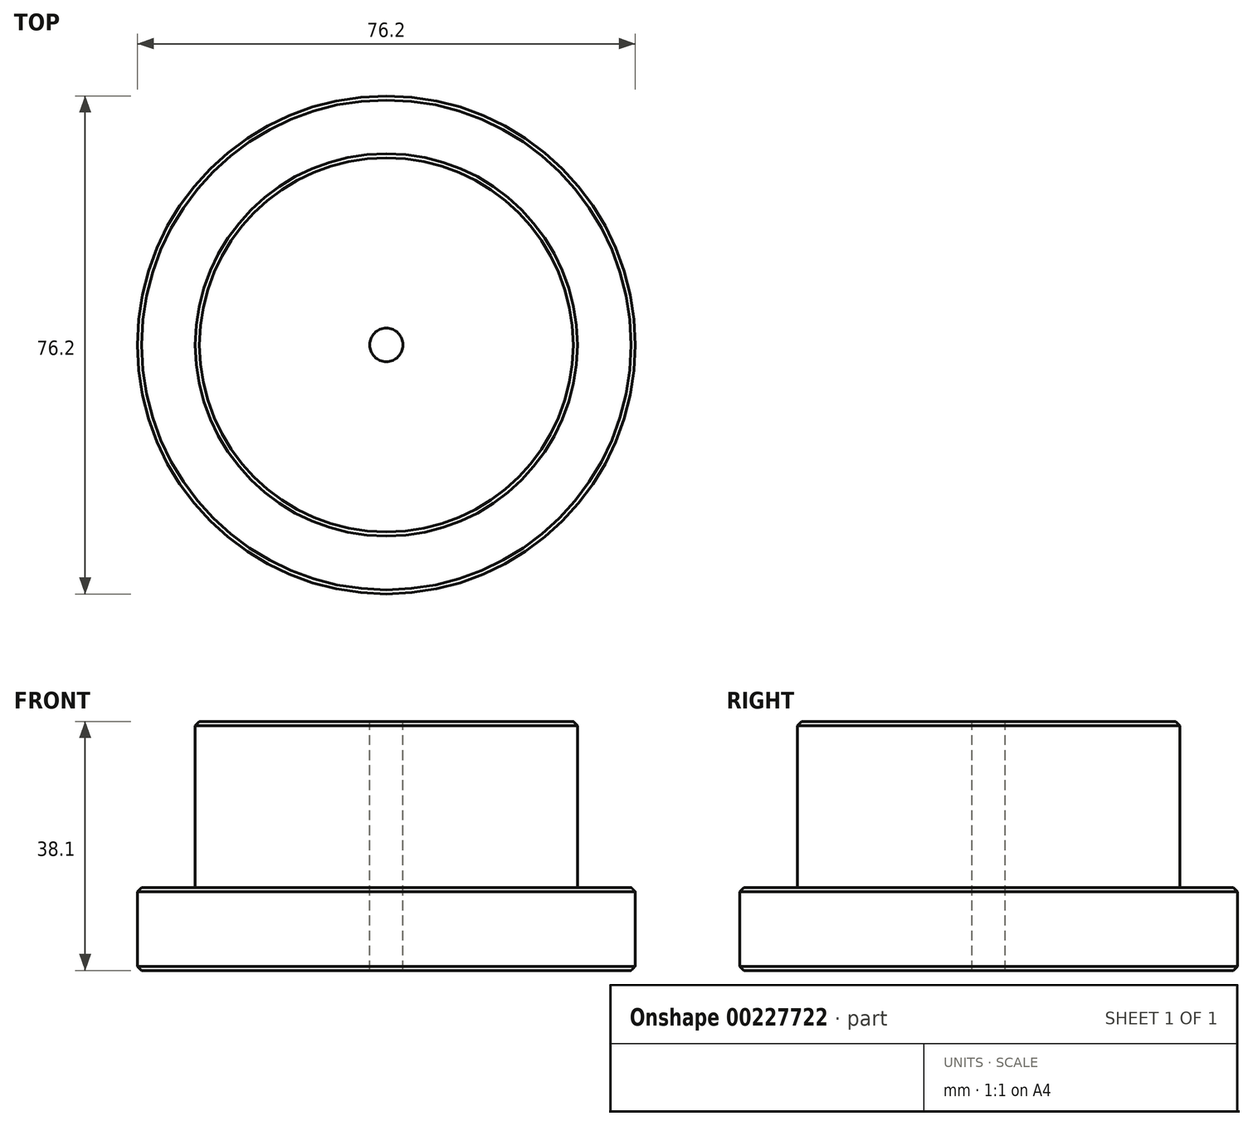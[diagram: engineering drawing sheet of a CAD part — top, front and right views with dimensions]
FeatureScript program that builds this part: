
annotation { "Feature Type Name" : "Feature", "Feature Type Description" : "" }
export const myFeature = defineFeature(function(context is Context, id is Id, definition is map)
    precondition{}
    {
        {
            var Q0;
            Q0=qCreatedBy(makeId("Top.planeOp"),FACE);
            var sketch = newSketch(context, id + "F0", { "sketchPlane" : qUnion([Q0])});
            skCircle(sketch, "E0", {"center": v(0, 0) * mm, "radius": 38.1 * mm});
            skSolve(sketch);
        }
        {
            var Q0;
            Q0 = qSketchRegion(id + "F0", true);
            extrude(context, id + "F1", {"entities" : qUnion([Q0]), "depth" : 12.7 * mm});
        }
        {
            var Q0;
            Q0=makeQuery(id+"F1.opExtrude","CAP_FACE",FACE,{"disambiguationData":[OSD([sQuery(id+"F0.wireOp",EDGE,"E0")])],"isStart":false});
            var sketch = newSketch(context, id + "F2", { "sketchPlane" : qUnion([Q0])});
            skCircle(sketch, "E1", {"center": v(0, 0) * mm, "radius": 29.25 * mm});
            skSolve(sketch);
        }
        {
            var Q0;
            Q0 = qSketchRegion(id + "F2", true);
            extrude(context, id + "F3", {"entities" : qUnion([Q0]), "operationType" : NewBodyOperationType.ADD, "depth" : 25.4 * mm});
        }
        {
            var Q0;
            Q0=makeQuery(id+"F3.opExtrude","CAP_EDGE",EDGE,{"disambiguationData":[OSD([sQuery(id+"F2.wireOp",EDGE,"E1")])],"isStart":false});
            var Q1;
            Q1=makeQuery(id+"F1.opExtrude","CAP_EDGE",EDGE,{"disambiguationData":[OSD([sQuery(id+"F0.wireOp",EDGE,"E0")])],"isStart":false});
            var Q2;
            Q2=makeQuery(id+"F1.opExtrude","CAP_EDGE",EDGE,{"disambiguationData":[OSD([sQuery(id+"F0.wireOp",EDGE,"E0")])],"isStart":true});
            chamfer(context, id + "F4", {"entities" : qUnion([Q0, Q1, Q2]), "width" : 0.64 * mm, "tangentPropagation" : true});
        }
        {
            var Q0;
            Q0=makeQuery(id+"F3.opExtrude","CAP_FACE",FACE,{"disambiguationData":[OSD([sQuery(id+"F2.wireOp",EDGE,"E1")])],"isStart":false});
            var sketch = newSketch(context, id + "F5", { "sketchPlane" : qUnion([Q0])});
            skPoint(sketch, "E2", {"position": v(0, 0) * mm});
            skSolve(sketch);
        }
        {
            var Q0;
            Q0=sQuery(id+"F5.wireOp",VERTEX,"E2");
            var Q1;
            Q1=makeQuery(id+"F1.opExtrude","SWEPT_BODY",BODY,{"disambiguationData":[OSD([sQuery(id+"F0.wireOp",EDGE,"E0")])]});
            hole(context, id + "F6", {"style" : HoleStyle.SIMPLE, "endStyle" : HoleEndStyle.THROUGH, "standardTappedOrClearance" : lookupTablePath({ "standard" : "ANSI", "engagement" : "75%", "pitch" : "20 tpi", "size" : "1/4", "type" : "Tapped" }), "standardBlindInLast" : lookupTablePath({ "standard" : "ANSI", "engagement" : "75%", "pitch" : "20 tpi", "size" : "1/4", "type" : "Tapped" }), "holeDiameter" : 5.1 * mm, "locations" : qUnion([Q0]), "scope" : qUnion([Q1]), "isTappedThrough" : true, "majorDiameter" : 6.35 * mm, "showTappedDepth" : true});
        }
    });
